MODEL slx_3052872beab5
KIND model
CONFIG AbsTol = auto
CONFIG FixedStep = auto
CONFIG InitFcn = clear functions
CONFIG MaxStep = auto
CONFIG MinStep = auto
CONFIG RelTol = 1e-3
CONFIG SampleTimeConstraint = Unconstrained
CONFIG Solver = ode45
CONFIG SolverMode = Auto
CONFIG SolverName = ode45
CONFIG StartTime = 0.0
CONFIG StopTime = 2
BLOCK [Clock] Clock
BLOCK [Constant] Constant1
  Value = 20
BLOCK [Demux] Demux
  DisplayOption = bar
  Outputs = 2
  Ports = [1, 2]
BLOCK [Display] Display
  Decimation = 1
  Ports = [1]
BLOCK [Mux] Mux1
  DisplayOption = bar
  Inputs = 2
  Ports = [2, 1]
BLOCK [Mux] Mux2
  DisplayOption = bar
  Inputs = 2
  Ports = [2, 1]
BLOCK [Scope] Network Schedule
  Ports = [1]
  ScopeSpecificationString = Simulink.scopes.TimeScopeBlockCfg('CurrentConfiguration', extmgr.ConfigurationSet(extmgr.Configuration('Core','General UI',true,'FigureColor',[0.156862745098039 0.156862745098039 0.156862745098039]),extmgr.Configuration('Core','Source UI',true),extmgr.Configuration('Sources','WiredSimulink',true,'DataLogging',true,'DataLoggingVariableName','nschedule','DataLoggingSaveFormat','StructureWithTime','D...<+2849ch>
BLOCK [Reference] Regulator Node  REF=truetime/TrueTime Kernel  (lib defined in slx_0362a698a4ec)
  Ports = [1, 1]
  SourceBlock = truetime/TrueTime Kernel
BLOCK [Scope] Schedule, actuator node
  Ports = [1]
  ScopeSpecificationString = Simulink.scopes.TimeScopeBlockCfg('CurrentConfiguration', extmgr.ConfigurationSet(extmgr.Configuration('Core','General UI',true,'FigureColor',[0.156862745098039 0.156862745098039 0.156862745098039]),extmgr.Configuration('Core','Source UI',true),extmgr.Configuration('Sources','WiredSimulink',true,'DataLoggingSaveFormat','Array','DataLoggingDecimation','1','DataLoggingDecimateData',true),extmgr.Conf...<+2722ch>
BLOCK [Scope] Schedule, computer node
  Ports = [1]
  ScopeSpecificationString = Simulink.scopes.TimeScopeBlockCfg('CurrentConfiguration', extmgr.ConfigurationSet(extmgr.Configuration('Core','General UI',true,'FigureColor',[0.156862745098039 0.156862745098039 0.156862745098039]),extmgr.Configuration('Core','Source UI',true),extmgr.Configuration('Sources','WiredSimulink',true,'DataLogging',true,'DataLoggingVariableName','schedule','DataLoggingSaveFormat','StructureWithTime','Da...<+2861ch>
BLOCK [Reference] Sensor//Actuator Node  REF=truetime/TrueTime Kernel  (lib defined in slx_0362a698a4ec)
  Ports = [1, 2]
  SourceBlock = truetime/TrueTime Kernel
BLOCK [StateSpace] State-Space
  A = [0 1; 0 -1]
  B = [0 1000]'
  C = [1 0; 0 1]
  D = [0 0]'
  Ports = [1, 1]
  X0 = [1 1]'
BLOCK [Reference] TrueTime Wireless Network  REF=truetime/TrueTime Wireless   (lib defined in slx_0362a698a4ec)
Network
  Ports = [2, 1]
  SourceBlock = truetime/TrueTime Wireless \nNetwork
  SourceType = Wireless Network
BLOCK [Constant] X
  Value = 0
BLOCK [ZeroOrderHold] Zero-Order Hold
  SampleTime = 0.01
BLOCK [Scope] r, y
  NumInputPorts = 3
  Ports = [3]
  ScopeSpecificationString = Simulink.scopes.TimeScopeBlockCfg('CurrentConfiguration', extmgr.ConfigurationSet(extmgr.Configuration('Core','General UI',true,'FigureColor',[1 1 1]),extmgr.Configuration('Core','Source UI',true),extmgr.Configuration('Sources','WiredSimulink',true,'DataLoggingVariableName','y','DataLoggingSaveFormat','StructureWithTime','DataLoggingDecimation','1','DataLoggingDecimateData',true),extmgr.Configurat...<+4735ch>
BLOCK [DiscretePulseGenerator] reference
  Period = 1.2
  Ports = [0, 1]
  PulseType = Time based
  PulseWidth = 50
ANNOTATION (root): TrueTime 2.0 Wireless Battery-Powered Control System <copyright redacted>
ANNOTATION (root): u
ANNOTATION (root): y
LINE Clock:1 -> Display:1
LINE Constant1:1 -> Mux2:2
LINE Demux:1 -> r, y:1
LINE Demux:2 -> r, y:2
LINE Mux1:1 -> TrueTime Wireless Network:1
LINE Mux2:1 -> TrueTime Wireless Network:2
LINE Regulator Node:1 -> Schedule, computer node:1
LINE Sensor//Actuator Node:1 -> Zero-Order Hold:1
LINE Sensor//Actuator Node:2 -> Schedule, actuator node:1
NET State-Space:1 -> Demux:1, Sensor//Actuator Node:1
LINE TrueTime Wireless Network:1 -> Network Schedule:1
NET X:1 -> Mux1:1, Mux1:2, Mux2:1
NET Zero-Order Hold:1 -> State-Space:1, r, y:3
LINE reference:1 -> Regulator Node:1
note: NET lines group one-source signal fan-out (src -> all destinations, sorted); 1:1 wires keep LINE
